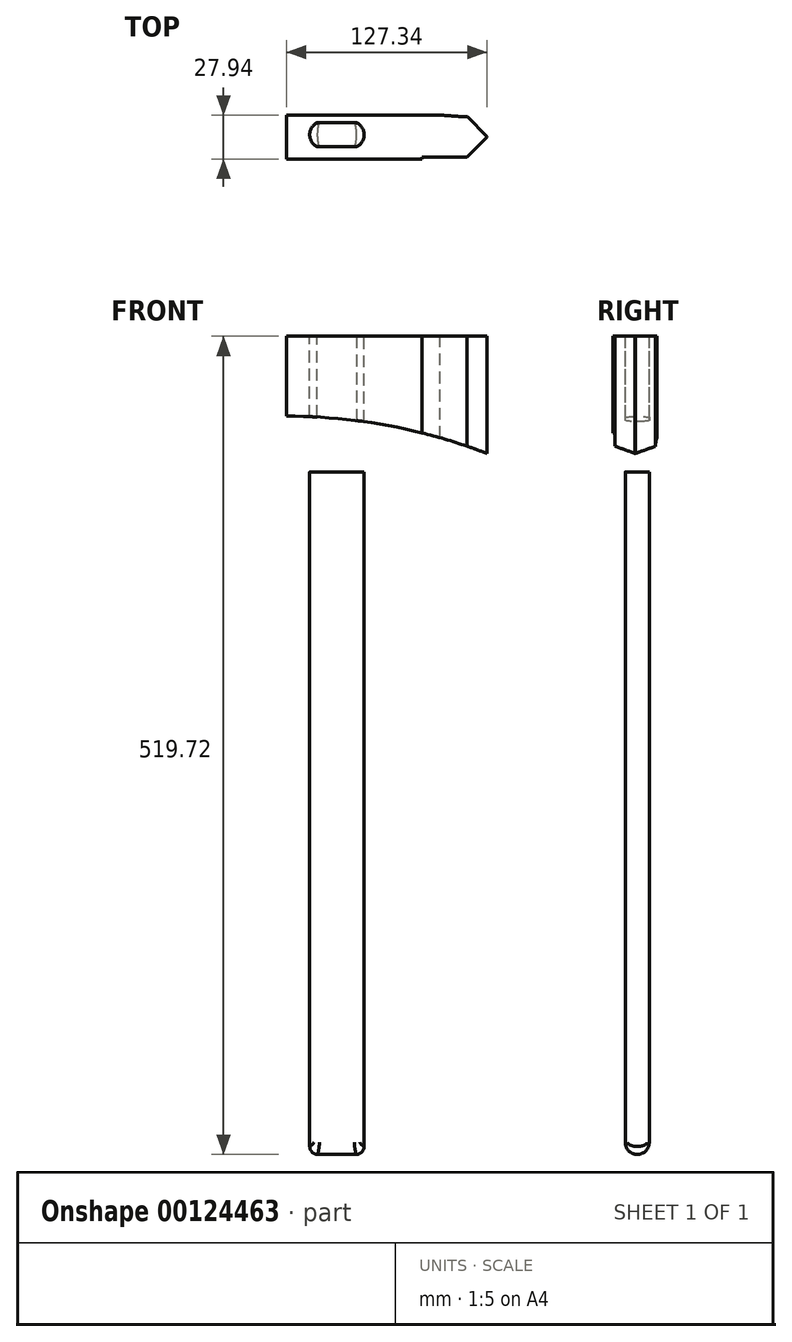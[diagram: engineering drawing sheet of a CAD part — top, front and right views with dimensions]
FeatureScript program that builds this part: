
annotation { "Feature Type Name" : "Feature", "Feature Type Description" : "" }
export const myFeature = defineFeature(function(context is Context, id is Id, definition is map)
    precondition{}
    {
        {
            var Q0;
            Q0=qCreatedBy(makeId("Front.planeOp"),FACE);
            var sketch = newSketch(context, id + "F0", { "sketchPlane" : qUnion([Q0])});
            skLineSegment(sketch, "E0", {"start": v(-62.65, 67.38) * mm, "end": v(-62.65, 16.58) * mm});
            skArc(sketch, "E1", {"start": v(64.69, -7.1) * mm, "mid": v(2.1, 10.6) * mm, "end": v(-62.65, 16.58) * mm});
            skLineSegment(sketch, "E2", {"start": v(-62.65, 67.38) * mm, "end": v(64.69, 67.38) * mm});
            skLineSegment(sketch, "E3", {"start": v(64.69, 67.38) * mm, "end": v(64.69, -7.1) * mm});
            skPoint(sketch, "E4.end.orphan", {"position": v(64.69, 16.42) * mm});
            skLineSegment(sketch, "E5", {"start": v(23.46, 5.95) * mm, "end": v(23.46, 67.38) * mm});
            skSolve(sketch);
        }
        {
            var Q0;
            {var subQ0=sQuery(id+"F0.wireOp",EDGE,"E0");Q0=makeQuery(id+"F0.imprint","IMPRINT",FACE,{"disambiguationData":[TD([[makeQuery(id+"F0.imprint","IMPRINT",EDGE,{"derivedFrom":subQ0}),1.0]])]});}
            extrude(context, id + "F1", {"entities" : qUnion([Q0]), "endBound" : BoundingType.SYMMETRIC, "depth" : 27.94 * mm});
        }
        {
            var Q0;
            {var subQ0=sQuery(id+"F0.wireOp",EDGE,"E3");Q0=makeQuery(id+"F0.imprint","IMPRINT",FACE,{"disambiguationData":[TD([[makeQuery(id+"F0.imprint","IMPRINT",EDGE,{"derivedFrom":subQ0}),-1.0]])]});}
            extrude(context, id + "F2", {"entities" : qUnion([Q0]), "operationType" : NewBodyOperationType.ADD, "endBound" : BoundingType.SYMMETRIC, "depth" : 25.4 * mm});
        }
        {
            var Q0;
            Q0=makeQuery(id+"F2.opExtrude","CAP_EDGE",EDGE,{"disambiguationData":[OSD([sQuery(id+"F0.wireOp",EDGE,"E5")])],"isStart":false});
            var Q1;
            Q1=makeQuery(id+"F2.opExtrude","CAP_EDGE",EDGE,{"disambiguationData":[OSD([sQuery(id+"F0.wireOp",EDGE,"E5")])],"isStart":true});
            chamfer(context, id + "F3", {"entities" : qUnion([Q0, Q1]), "width" : 12.7 * mm, "tangentPropagation" : true});
        }
        {
            var Q0;
            {var subQ0=sQuery(id+"F0.wireOp",EDGE,"E5");Q0=makeQuery(id+"F3.opChamfer","BLEND_EDGE",EDGE,{"blendedFrom":[makeQuery(id+"F2.opExtrude","CAP_EDGE",EDGE,{"disambiguationData":[OSD([subQ0])],"isStart":true}),makeQuery(id+"F2.opExtrude","CAP_FACE",FACE,{"disambiguationData":[OSD([sQuery(id+"F0.wireOp",EDGE,"E1"),sQuery(id+"F0.wireOp",EDGE,"E2"),sQuery(id+"F0.wireOp",EDGE,"E3"),subQ0])],"isStart":true})],"blendedInto":[makeQuery(id+"F2.opExtrude","CAP_FACE",FACE,{"disambiguationData":[OSD([sQuery(id+"F0.wireOp",EDGE,"E1"),sQuery(id+"F0.wireOp",EDGE,"E2"),sQuery(id+"F0.wireOp",EDGE,"E3"),subQ0])],"isStart":true})]});}
            var Q1;
            {var subQ0=sQuery(id+"F0.wireOp",EDGE,"E5");Q1=makeQuery(id+"F3.opChamfer","BLEND_EDGE",EDGE,{"blendedFrom":[makeQuery(id+"F2.opExtrude","CAP_EDGE",EDGE,{"disambiguationData":[OSD([subQ0])],"isStart":false}),makeQuery(id+"F2.opExtrude","CAP_FACE",FACE,{"disambiguationData":[OSD([sQuery(id+"F0.wireOp",EDGE,"E1"),sQuery(id+"F0.wireOp",EDGE,"E2"),sQuery(id+"F0.wireOp",EDGE,"E3"),subQ0])],"isStart":false})],"blendedInto":[makeQuery(id+"F2.opExtrude","CAP_FACE",FACE,{"disambiguationData":[OSD([sQuery(id+"F0.wireOp",EDGE,"E1"),sQuery(id+"F0.wireOp",EDGE,"E2"),sQuery(id+"F0.wireOp",EDGE,"E3"),subQ0])],"isStart":false})]});}
            fillet(context, id + "F4", {"entities" : qUnion([Q0, Q1]), "radius" : 341.47 * mm, "tangentPropagation" : true, "allowEdgeOverflow" : false});
        }
        {
            var Q0;
            Q0=makeQuery(id+"F2.opExtrude","CAP_EDGE",EDGE,{"disambiguationData":[OSD([sQuery(id+"F0.wireOp",EDGE,"E3")])],"isStart":true});
            var Q1;
            Q1=makeQuery(id+"F2.opExtrude","CAP_EDGE",EDGE,{"disambiguationData":[OSD([sQuery(id+"F0.wireOp",EDGE,"E3")])],"isStart":false});
            chamfer(context, id + "F5", {"entities" : qUnion([Q0, Q1]), "width" : 12.7 * mm, "tangentPropagation" : true});
        }
        {
            var Q0;
            {var subQ0=sQuery(id+"F0.wireOp",EDGE,"E2");Q0=makeQuery(id+"F2.boolean.opBoolean","MERGE",FACE,{"derivedFrom":[makeQuery(id+"F1.opExtrude","SWEPT_FACE",FACE,{"disambiguationData":[OSD([subQ0])]}),makeQuery(id+"F2.opExtrude","SWEPT_FACE",FACE,{"disambiguationData":[OSD([subQ0])]})]});}
            var sketch = newSketch(context, id + "F6", { "sketchPlane" : qUnion([Q0])});
            skLineSegment(sketch, "E6", {"start": v(-43.33, -6.13) * mm, "end": v(-17.93, -6.13) * mm});
            skLineSegment(sketch, "E7", {"start": v(-17.93, 9.1) * mm, "end": v(-43.33, 9.1) * mm});
            skArc(sketch, "E8", {"start": v(-43.33, 9.1) * mm, "mid": v(-47.9, 1.49) * mm, "end": v(-43.33, -6.13) * mm});
            skArc(sketch, "E9", {"start": v(-17.93, -6.13) * mm, "mid": v(-13.37, 1.49) * mm, "end": v(-17.93, 9.1) * mm});
            skSolve(sketch);
        }
        {
            var Q0;
            Q0 = qSketchRegion(id + "F6", true);
            extrude(context, id + "F7", {"entities" : qUnion([Q0]), "oppositeDirection" : true, "depth" : 519.72 * mm});
        }
        {
            var Q0;
            {var subQ0=sQuery(id+"F0.wireOp",EDGE,"E2");Q0=makeQuery(id+"F2.boolean.opBoolean","MERGE",FACE,{"derivedFrom":[makeQuery(id+"F1.opExtrude","SWEPT_FACE",FACE,{"disambiguationData":[OSD([subQ0])]}),makeQuery(id+"F2.opExtrude","SWEPT_FACE",FACE,{"disambiguationData":[OSD([subQ0])]})]});}
            var sketch = newSketch(context, id + "F8", { "sketchPlane" : qUnion([Q0])});
            skLineSegment(sketch, "E10.0", {"start": v(-43.33, -6.13) * mm, "end": v(-17.93, -6.13) * mm});
            skArc(sketch, "E10.1", {"start": v(-17.93, -6.13) * mm, "mid": v(-13.37, 1.49) * mm, "end": v(-17.93, 9.1) * mm});
            skArc(sketch, "E10.2", {"start": v(-43.33, 9.1) * mm, "mid": v(-47.9, 1.49) * mm, "end": v(-43.33, -6.13) * mm});
            skLineSegment(sketch, "E10.3", {"start": v(-17.93, 9.1) * mm, "end": v(-43.33, 9.1) * mm});
            skSolve(sketch);
        }
        {
            var Q0;
            Q0 = qSketchRegion(id + "F8", true);
            extrude(context, id + "F9", {"entities" : qUnion([Q0]), "operationType" : NewBodyOperationType.REMOVE, "oppositeDirection" : true, "depth" : 86.15 * mm});
        }
        {
            var Q0;
            Q0=makeQuery(id+"F7.opExtrude","CAP_EDGE",EDGE,{"disambiguationData":[OSD([sQuery(id+"F6.wireOp",EDGE,"E7")])],"isStart":false});
            var Q1;
            Q1=makeQuery(id+"F7.opExtrude","CAP_EDGE",EDGE,{"disambiguationData":[OSD([sQuery(id+"F6.wireOp",EDGE,"E6")])],"isStart":false});
            fillet(context, id + "F10", {"entities" : qUnion([Q0, Q1]), "radius" : 7.62 * mm, "tangentPropagation" : true, "allowEdgeOverflow" : false});
        }
        {
            var Q0;
            Q0=makeQuery(id+"F10.opFillet","BLEND_EDGE",EDGE,{"blendedFrom":[makeQuery(id+"F7.opExtrude","CAP_EDGE",EDGE,{"disambiguationData":[OSD([sQuery(id+"F6.wireOp",EDGE,"E7")])],"isStart":false}),makeQuery(id+"F7.opExtrude","SWEPT_FACE",FACE,{"disambiguationData":[OSD([sQuery(id+"F6.wireOp",EDGE,"E8")])]})],"blendedInto":[makeQuery(id+"F7.opExtrude","SWEPT_FACE",FACE,{"disambiguationData":[OSD([sQuery(id+"F6.wireOp",EDGE,"E8")])]})]});
            var Q1;
            Q1=makeQuery(id+"F10.opFillet","BLEND_EDGE",EDGE,{"blendedFrom":[makeQuery(id+"F7.opExtrude","CAP_EDGE",EDGE,{"disambiguationData":[OSD([sQuery(id+"F6.wireOp",EDGE,"E7")])],"isStart":false}),makeQuery(id+"F7.opExtrude","SWEPT_FACE",FACE,{"disambiguationData":[OSD([sQuery(id+"F6.wireOp",EDGE,"E9")])]})],"blendedInto":[makeQuery(id+"F7.opExtrude","SWEPT_FACE",FACE,{"disambiguationData":[OSD([sQuery(id+"F6.wireOp",EDGE,"E9")])]})]});
            fillet(context, id + "F11", {"entities" : qUnion([Q0, Q1]), "radius" : 5.08 * mm, "tangentPropagation" : true, "allowEdgeOverflow" : false});
        }
    });
